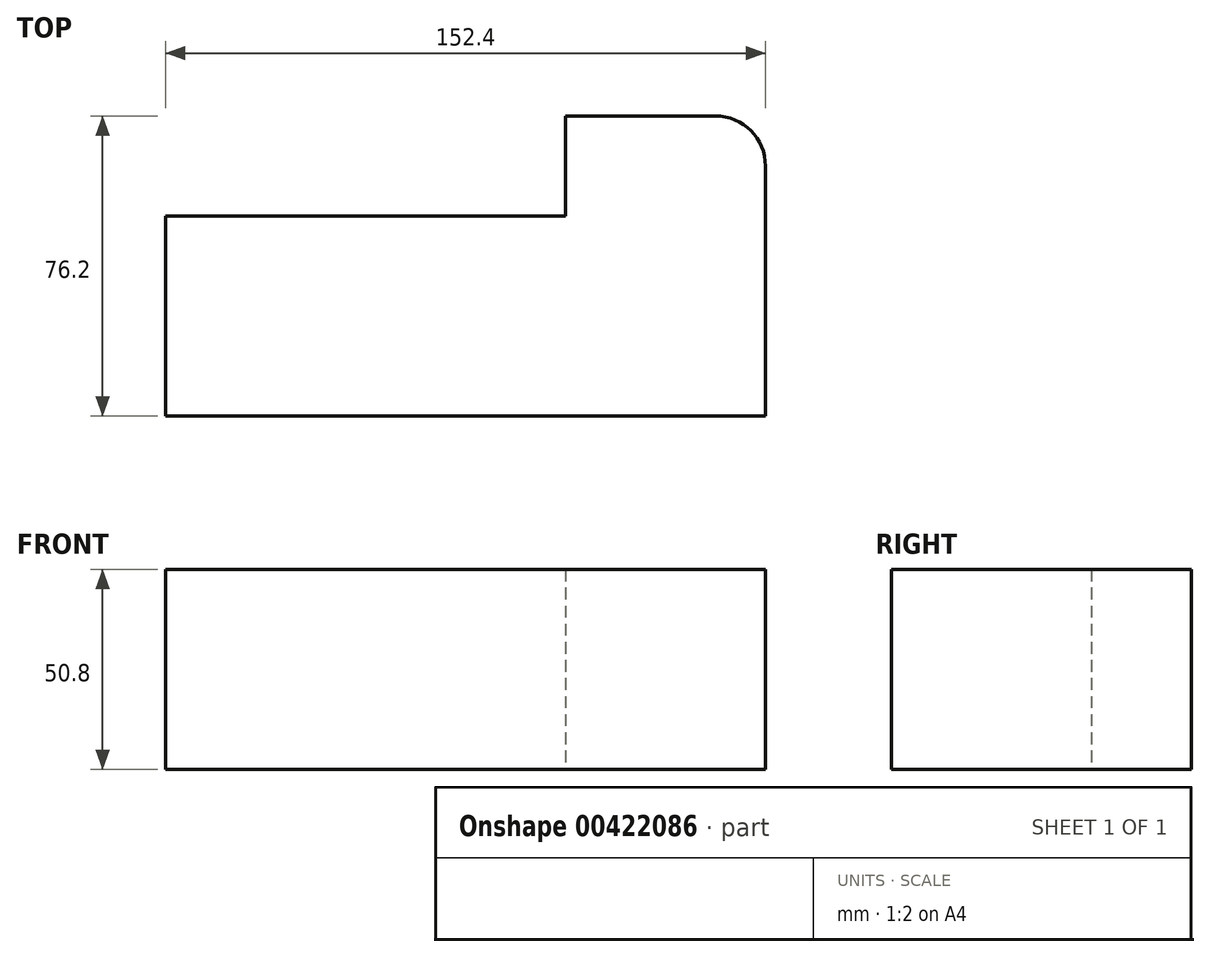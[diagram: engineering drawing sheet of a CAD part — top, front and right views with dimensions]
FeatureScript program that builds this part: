
annotation { "Feature Type Name" : "Feature", "Feature Type Description" : "" }
export const myFeature = defineFeature(function(context is Context, id is Id, definition is map)
    precondition{}
    {
        {
            var Q0;
            Q0=qCreatedBy(makeId("Top.planeOp"),FACE);
            var sketch = newSketch(context, id + "F0", { "sketchPlane" : qUnion([Q0])});
            skLineSegment(sketch, "E0", {"start": v(0, 0) * mm, "end": v(152.4, 0) * mm});
            skLineSegment(sketch, "E1", {"start": v(0, 0) * mm, "end": v(0, 50.8) * mm});
            skLineSegment(sketch, "E2", {"start": v(0, 50.8) * mm, "end": v(101.6, 50.8) * mm});
            skLineSegment(sketch, "E3", {"start": v(101.6, 50.8) * mm, "end": v(101.6, 76.2) * mm});
            skLineSegment(sketch, "E4", {"start": v(101.6, 76.2) * mm, "end": v(152.4, 76.2) * mm});
            skLineSegment(sketch, "E5", {"start": v(152.4, 76.2) * mm, "end": v(152.4, 0) * mm});
            skSolve(sketch);
        }
        {
            var Q0;
            Q0 = qSketchRegion(id + "F0", true);
            extrude(context, id + "F1", {"entities" : qUnion([Q0]), "depth" : 50.8 * mm});
        }
        {
            var Q0;
            Q0=makeQuery(id+"F1.opExtrude","SWEPT_EDGE",EDGE,{"disambiguationData":[OSD([sQuery(id+"F0.wireOp",EDGE,"E4"),sQuery(id+"F0.wireOp",EDGE,"E5")])]});
            fillet(context, id + "F2", {"entities" : qUnion([Q0]), "radius" : 12.7 * mm, "tangentPropagation" : true, "allowEdgeOverflow" : false});
        }
    });
